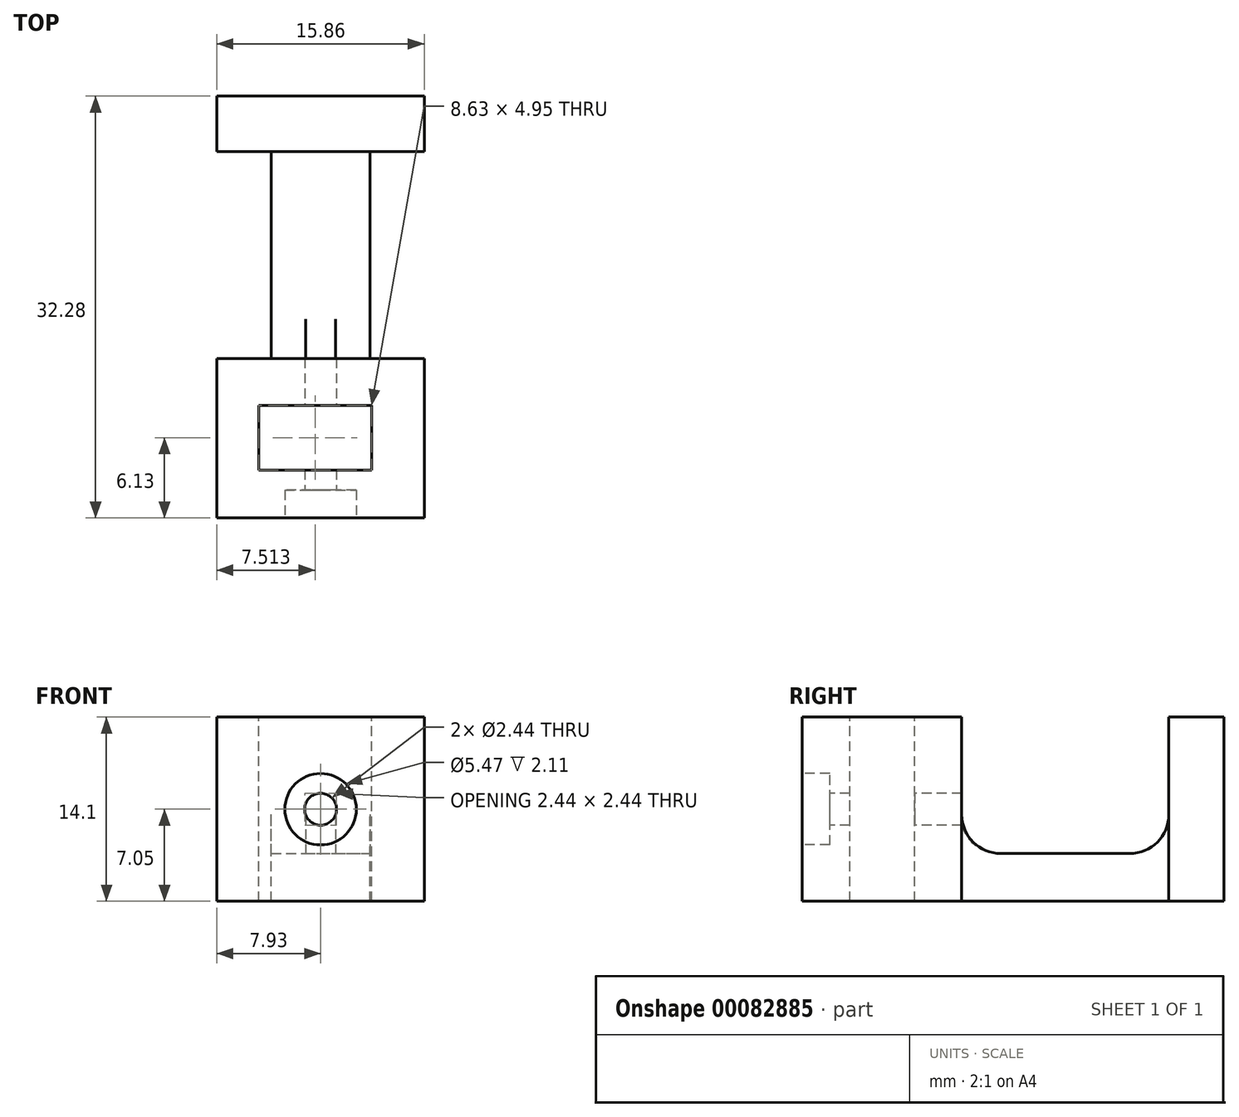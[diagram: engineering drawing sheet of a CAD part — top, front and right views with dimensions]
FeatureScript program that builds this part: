
annotation { "Feature Type Name" : "Feature", "Feature Type Description" : "" }
export const myFeature = defineFeature(function(context is Context, id is Id, definition is map)
    precondition{}
    {
        {
            var Q0;
            Q0=qCreatedBy(makeId("Top.planeOp"),FACE);
            var sketch = newSketch(context, id + "F0", { "sketchPlane" : qUnion([Q0])});
            skLineSegment(sketch, "E0.bottom", {"start": v(7.94, 16.14) * mm, "end": v(-7.93, 16.14) * mm});
            skLineSegment(sketch, "E0.top", {"start": v(7.93, -16.14) * mm, "end": v(-7.94, -16.14) * mm});
            skLineSegment(sketch, "E0.left", {"start": v(7.94, 16.14) * mm, "end": v(7.93, -16.14) * mm});
            skLineSegment(sketch, "E0.right", {"start": v(-7.93, 16.14) * mm, "end": v(-7.94, -16.14) * mm});
            skPoint(sketch, "E0.middle", {"position": v(0, 0) * mm});
            skSolve(sketch);
        }
        {
            var Q0;
            Q0=qSketchRegion(id+"F0",true);
            extrude(context, id + "F1", {"entities" : qUnion([Q0]), "depth" : 14.1 * mm});
        }
        {
            var Q0;
            Q0=makeQuery(id+"F1.opExtrude","CAP_FACE",FACE,{"disambiguationData":[OSD([sQuery(id+"F0.wireOp",EDGE,"E0.bottom"),sQuery(id+"F0.wireOp",EDGE,"E0.top"),sQuery(id+"F0.wireOp",EDGE,"E0.left"),sQuery(id+"F0.wireOp",EDGE,"E0.right")])],"isStart":false});
            var sketch = newSketch(context, id + "F2", { "sketchPlane" : qUnion([Q0])});
            skLineSegment(sketch, "E1.bottom", {"start": v(-7.93, 11.9) * mm, "end": v(7.94, 11.9) * mm});
            skLineSegment(sketch, "E1.top", {"start": v(-7.93, -3.94) * mm, "end": v(7.94, -3.94) * mm});
            skLineSegment(sketch, "E1.left", {"start": v(-7.93, 11.9) * mm, "end": v(-7.93, -3.94) * mm});
            skLineSegment(sketch, "E1.right", {"start": v(7.94, 11.9) * mm, "end": v(7.94, -3.94) * mm});
            skSolve(sketch);
        }
        {
            var Q0;
            Q0=qSketchRegion(id+"F2",true);
            extrude(context, id + "F3", {"entities" : qUnion([Q0]), "operationType" : NewBodyOperationType.REMOVE, "oppositeDirection" : true, "depth" : 10.45 * mm});
        }
        {
            var Q0;
            Q0=makeQuery(id+"F3.boolean.opBoolean","COPY",FACE,{"derivedFrom":makeQuery(id+"F3.opExtrude","CAP_FACE",FACE,{"disambiguationData":[OSD([sQuery(id+"F2.wireOp",EDGE,"E1.bottom"),sQuery(id+"F2.wireOp",EDGE,"E1.top"),sQuery(id+"F2.wireOp",EDGE,"E1.left"),sQuery(id+"F2.wireOp",EDGE,"E1.right")])],"isStart":false})});
            var sketch = newSketch(context, id + "F4", { "sketchPlane" : qUnion([Q0])});
            skLineSegment(sketch, "E2.bottom", {"start": v(3.77, 11.9) * mm, "end": v(7.93, 11.9) * mm});
            skLineSegment(sketch, "E2.top", {"start": v(3.77, -3.94) * mm, "end": v(7.93, -3.94) * mm});
            skLineSegment(sketch, "E2.left", {"start": v(3.77, 11.9) * mm, "end": v(3.78, -3.94) * mm});
            skLineSegment(sketch, "E2.right", {"start": v(7.94, 11.9) * mm, "end": v(7.94, -3.94) * mm});
            skLineSegment(sketch, "E3.bottom", {"start": v(-7.93, 11.9) * mm, "end": v(-3.77, 11.9) * mm});
            skLineSegment(sketch, "E3.top", {"start": v(-7.93, -3.94) * mm, "end": v(-3.77, -3.94) * mm});
            skLineSegment(sketch, "E3.left", {"start": v(-7.93, 11.9) * mm, "end": v(-7.93, -3.94) * mm});
            skLineSegment(sketch, "E3.right", {"start": v(-3.77, 11.9) * mm, "end": v(-3.77, -3.94) * mm});
            skSolve(sketch);
        }
        {
            var Q0;
            Q0=qSketchRegion(id+"F4",true);
            extrude(context, id + "F5", {"entities" : qUnion([Q0]), "operationType" : NewBodyOperationType.REMOVE, "endBound" : BoundingType.UP_TO_NEXT, "oppositeDirection" : true, "depth" : 25 * mm});
        }
        {
            var Q0;
            {var subQ0=sQuery(id+"F0.wireOp",EDGE,"E0.top");var subQ1=sQuery(id+"F0.wireOp",EDGE,"E0.left");var subQ2=sQuery(id+"F0.wireOp",EDGE,"E0.right");Q0=makeQuery(id+"F3.boolean.opBoolean","SPLIT",FACE,{"disambiguationData":[TD([makeQuery(id+"F1.opExtrude","SWEPT_FACE",FACE,{"disambiguationData":[OSD([subQ0])]})])],"derivedFrom":makeQuery(id+"F1.opExtrude","CAP_FACE",FACE,{"disambiguationData":[OSD([sQuery(id+"F0.wireOp",EDGE,"E0.bottom"),subQ0,subQ1,subQ2])],"isStart":false})});}
            var sketch = newSketch(context, id + "F6", { "sketchPlane" : qUnion([Q0])});
            skLineSegment(sketch, "E4.bottom", {"start": v(3.9, -12.49) * mm, "end": v(-4.73, -12.49) * mm});
            skLineSegment(sketch, "E4.top", {"start": v(3.9, -7.54) * mm, "end": v(-4.73, -7.54) * mm});
            skLineSegment(sketch, "E4.left", {"start": v(3.9, -12.49) * mm, "end": v(3.9, -7.54) * mm});
            skLineSegment(sketch, "E4.right", {"start": v(-4.73, -12.49) * mm, "end": v(-4.73, -7.54) * mm});
            skSolve(sketch);
        }
        {
            var Q0;
            Q0=qSketchRegion(id+"F6",true);
            extrude(context, id + "F7", {"entities" : qUnion([Q0]), "operationType" : NewBodyOperationType.REMOVE, "endBound" : BoundingType.UP_TO_NEXT, "oppositeDirection" : true, "depth" : 25 * mm});
        }
        {
            var Q0;
            Q0=makeQuery(id+"F1.opExtrude","SWEPT_FACE",FACE,{"disambiguationData":[OSD([sQuery(id+"F0.wireOp",EDGE,"E0.top")])]});
            var sketch = newSketch(context, id + "F8", { "sketchPlane" : qUnion([Q0])});
            skCircle(sketch, "E5", {"center": v(0, 7.05) * mm, "radius": 1.22 * mm});
            skSolve(sketch);
        }
        {
            var Q0;
            Q0=qSketchRegion(id+"F8",true);
            extrude(context, id + "F9", {"entities" : qUnion([Q0]), "operationType" : NewBodyOperationType.REMOVE, "oppositeDirection" : true, "depth" : 12.5 * mm});
        }
        {
            var Q0;
            Q0=makeQuery(id+"F1.opExtrude","SWEPT_FACE",FACE,{"disambiguationData":[OSD([sQuery(id+"F0.wireOp",EDGE,"E0.top")])]});
            var sketch = newSketch(context, id + "F10", { "sketchPlane" : qUnion([Q0])});
            skCircle(sketch, "E6", {"center": v(0, 7.05) * mm, "radius": 2.73 * mm});
            skSolve(sketch);
        }
        {
            var Q0;
            Q0=qSketchRegion(id+"F10",true);
            extrude(context, id + "F11", {"entities" : qUnion([Q0]), "operationType" : NewBodyOperationType.REMOVE, "oppositeDirection" : true, "depth" : 2.1 * mm});
        }
        {
            var Q0;
            Q0=makeQuery(id+"F3.boolean.opBoolean","COPY",EDGE,{"derivedFrom":makeQuery(id+"F3.opExtrude","CAP_EDGE",EDGE,{"disambiguationData":[OSD([sQuery(id+"F2.wireOp",EDGE,"E1.top")])],"isStart":false})});
            fillet(context, id + "F12", {"entities" : qUnion([Q0]), "radius" : 3 * mm, "tangentPropagation" : true, "allowEdgeOverflow" : false});
        }
        {
            var Q0;
            Q0=makeQuery(id+"F3.boolean.opBoolean","COPY",EDGE,{"derivedFrom":makeQuery(id+"F3.opExtrude","CAP_EDGE",EDGE,{"disambiguationData":[OSD([sQuery(id+"F2.wireOp",EDGE,"E1.bottom")])],"isStart":false})});
            fillet(context, id + "F13", {"entities" : qUnion([Q0]), "radius" : 3 * mm, "tangentPropagation" : true, "allowEdgeOverflow" : false});
        }
    });
